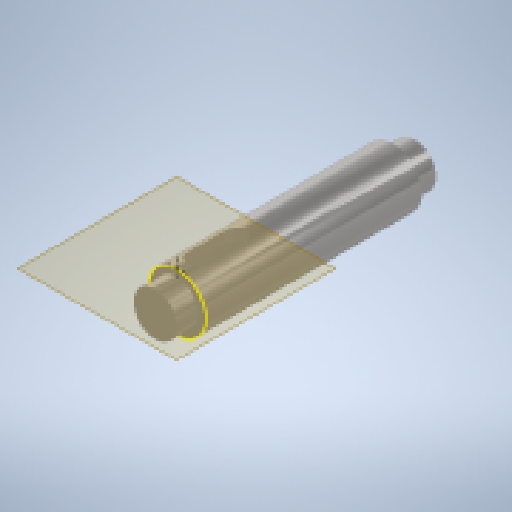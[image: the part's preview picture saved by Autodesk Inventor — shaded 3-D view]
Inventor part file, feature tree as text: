
AUTODESK INVENTOR PART (.ipt)
format: ipt  version: 2024 (Build 280153000, 153)  size: 184,832 bytes
history: native  units: mm
features: sketch x3, other x2, revolve x1, extrude x1
ambient origin geometry x8: Origin, YZ Plane, XZ Plane, XY Plane, X Axis, Y Axis, Z Axis, Center Point
bodies: Body1 (feature_tree)
feature tree (7):
  other  "ソリッド1"
  revolve  "回転1"
  sketch  "スケッチ2"
  other  "作業平面1"
  extrude  "押し出し1"  Depth=3.0mm
  sketch  "スケッチ1"
  sketch  "スケッチ3"
